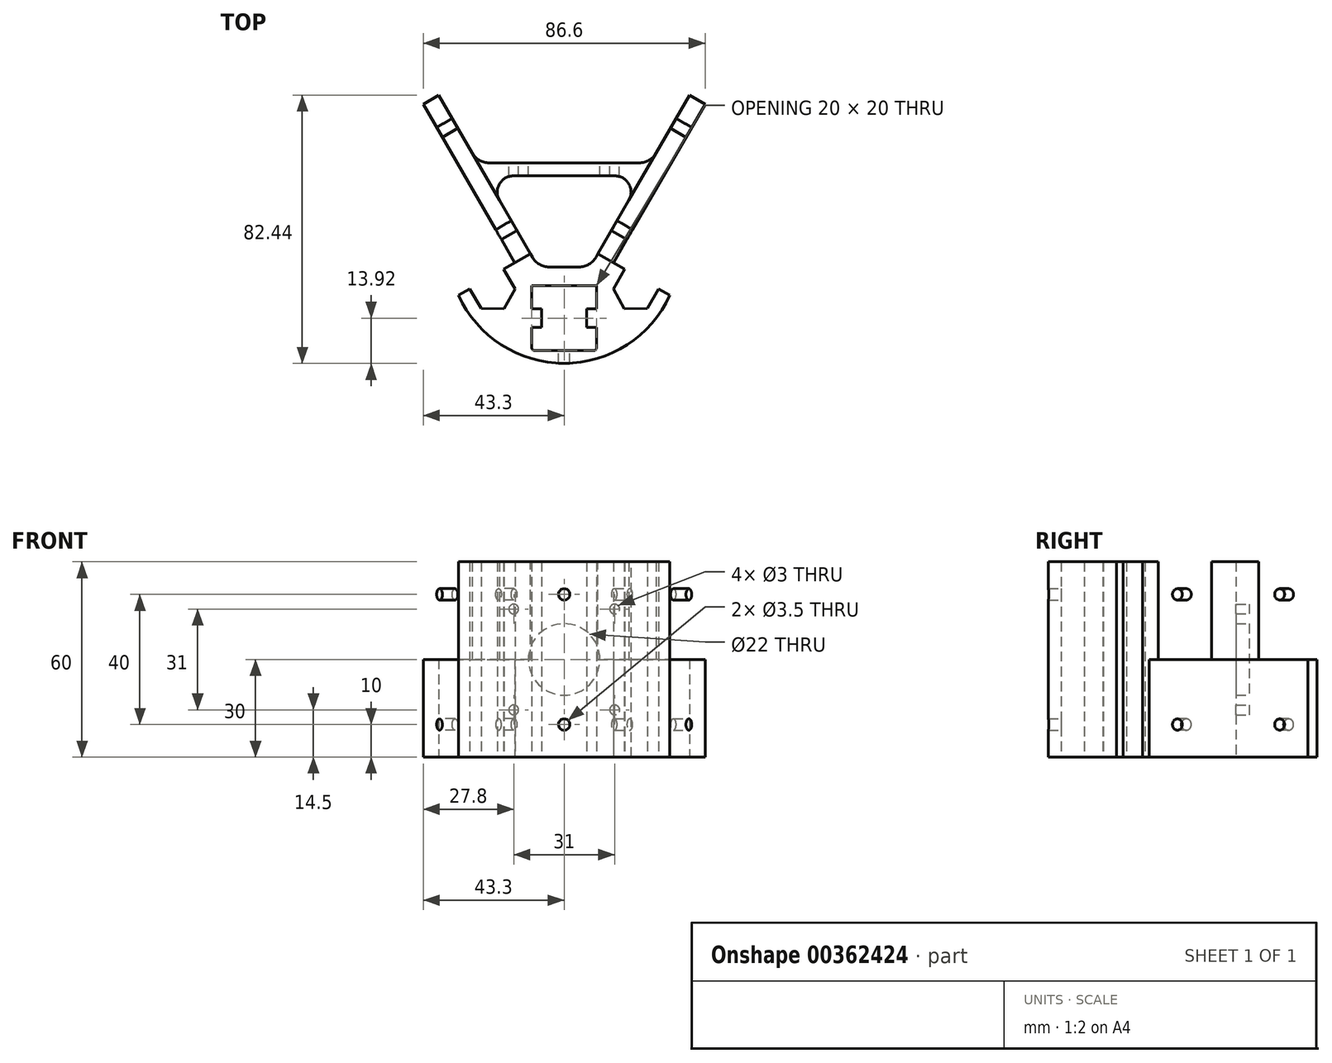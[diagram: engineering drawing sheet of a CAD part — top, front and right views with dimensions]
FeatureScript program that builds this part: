
annotation { "Feature Type Name" : "Feature", "Feature Type Description" : "" }
export const myFeature = defineFeature(function(context is Context, id is Id, definition is map)
    precondition{}
    {
        {
            var Q0;
            Q0=qCreatedBy(makeId("Top.planeOp"),FACE);
            var sketch = newSketch(context, id + "F0", { "sketchPlane" : qUnion([Q0])});
            skLineSegment(sketch, "E0", {"start": v(0, 0) * mm, "end": v(32.48, 0) * mm});
            skLineSegment(sketch, "E1", {"start": v(0, 0) * mm, "end": v(-32.48, 0) * mm});
            skArc(sketch, "E2", {"start": v(-32.48, 0) * mm, "mid": v(0, -20.94) * mm, "end": v(32.48, 0) * mm});
            skLineSegment(sketch, "E3", {"start": v(-32.48, 0) * mm, "end": v(-15.15, 10) * mm});
            skLineSegment(sketch, "E4", {"start": v(32.48, 0) * mm, "end": v(15.15, 10) * mm});
            skLineSegment(sketch, "E5", {"start": v(15.15, 10) * mm, "end": v(43.3, 58.75) * mm});
            skLineSegment(sketch, "E6", {"start": v(-15.15, 10) * mm, "end": v(-43.3, 58.75) * mm});
            skLineSegment(sketch, "E7", {"start": v(38.54, 61.5) * mm, "end": v(43.3, 58.75) * mm});
            skLineSegment(sketch, "E8.bottom", {"start": v(10, -17.02) * mm, "end": v(-10, -17.02) * mm});
            skLineSegment(sketch, "E8.top", {"start": v(10, 2.98) * mm, "end": v(-10, 2.98) * mm});
            skLineSegment(sketch, "E8.left", {"start": v(10, -17.02) * mm, "end": v(10, 2.98) * mm});
            skLineSegment(sketch, "E8.right", {"start": v(-10, -17.02) * mm, "end": v(-10, 2.98) * mm});
            skPoint(sketch, "E8.middle", {"position": v(0, -7.02) * mm});
            skLineSegment(sketch, "E9", {"start": v(-64.62, 8.7) * mm, "end": v(74.38, 8.7) * mm});
            skLineSegment(sketch, "E10", {"start": v(-43.3, 58.75) * mm, "end": v(-38.54, 61.5) * mm});
            skLineSegment(sketch, "E11", {"start": v(-38.54, 61.5) * mm, "end": v(-8.06, 8.7) * mm});
            skLineSegment(sketch, "E12", {"start": v(38.54, 61.5) * mm, "end": v(8.06, 8.7) * mm});
            skLineSegment(sketch, "E13", {"start": v(-64.62, 36.7) * mm, "end": v(67.86, 36.7) * mm});
            skLineSegment(sketch, "E14", {"start": v(-64.87, 40.7) * mm, "end": v(70.08, 40.7) * mm});
            skLineSegment(sketch, "E15.bottom", {"start": v(-10, -7.02) * mm, "end": v(-6.9, -7.02) * mm});
            skLineSegment(sketch, "E15.top", {"start": v(-10, -4.12) * mm, "end": v(-6.9, -4.12) * mm});
            skLineSegment(sketch, "E15.left", {"start": v(-10, -7.02) * mm, "end": v(-10, -4.12) * mm});
            skLineSegment(sketch, "E15.right", {"start": v(-6.9, -7.02) * mm, "end": v(-6.9, -4.12) * mm});
            skLineSegment(sketch, "E16.top", {"start": v(-10, -9.92) * mm, "end": v(-6.9, -9.92) * mm});
            skLineSegment(sketch, "E16.left", {"start": v(-10, -7.02) * mm, "end": v(-10, -9.92) * mm});
            skLineSegment(sketch, "E16.right", {"start": v(-6.9, -7.02) * mm, "end": v(-6.9, -9.92) * mm});
            skLineSegment(sketch, "E17.1.0", {"start": v(10, 2.98) * mm, "end": v(10, -17.02) * mm});
            skLineSegment(sketch, "E17.1.1", {"start": v(2.9, -17.02) * mm, "end": v(2.9, -13.92) * mm});
            skLineSegment(sketch, "E17.1.2", {"start": v(0, -17.02) * mm, "end": v(0, -13.92) * mm});
            skLineSegment(sketch, "E17.1.3", {"start": v(-2.9, -17.02) * mm, "end": v(-2.9, -13.92) * mm});
            skLineSegment(sketch, "E17.1.4", {"start": v(0, -13.92) * mm, "end": v(-2.9, -13.92) * mm});
            skLineSegment(sketch, "E17.1.5", {"start": v(0, -13.92) * mm, "end": v(2.9, -13.92) * mm});
            skLineSegment(sketch, "E17.2.0", {"start": v(-10, 2.98) * mm, "end": v(10, 2.98) * mm});
            skLineSegment(sketch, "E17.2.1", {"start": v(10, -4.12) * mm, "end": v(6.9, -4.12) * mm});
            skLineSegment(sketch, "E17.2.2", {"start": v(10, -7.02) * mm, "end": v(6.9, -7.02) * mm});
            skLineSegment(sketch, "E17.2.3", {"start": v(10, -9.92) * mm, "end": v(6.9, -9.92) * mm});
            skLineSegment(sketch, "E17.2.4", {"start": v(6.9, -7.02) * mm, "end": v(6.9, -9.92) * mm});
            skLineSegment(sketch, "E17.2.5", {"start": v(6.9, -7.02) * mm, "end": v(6.9, -4.12) * mm});
            skLineSegment(sketch, "E17.3.1", {"start": v(-2.9, 2.98) * mm, "end": v(-2.9, -0.12) * mm});
            skLineSegment(sketch, "E17.3.2", {"start": v(0, 2.98) * mm, "end": v(0, -0.12) * mm});
            skLineSegment(sketch, "E17.3.3", {"start": v(2.9, 2.98) * mm, "end": v(2.9, -0.12) * mm});
            skLineSegment(sketch, "E17.3.4", {"start": v(0, -0.12) * mm, "end": v(2.9, -0.12) * mm});
            skLineSegment(sketch, "E17.3.5", {"start": v(0, -0.12) * mm, "end": v(-2.9, -0.12) * mm});
            skLineSegment(sketch, "E18", {"start": v(18.62, 8) * mm, "end": v(15.12, 1.94) * mm});
            skLineSegment(sketch, "E19", {"start": v(29.01, 2) * mm, "end": v(25.51, -4.06) * mm});
            skPoint(sketch, "E20", {"position": v(23.81, 5) * mm});
            skLineSegment(sketch, "E21", {"start": v(15.12, 1.94) * mm, "end": v(18.51, -4.18) * mm});
            skLineSegment(sketch, "E22", {"start": v(25.51, -4.06) * mm, "end": v(18.51, -4.18) * mm});
            skLineSegment(sketch, "E23.MirrorCS", {"start": v(-18.62, 8) * mm, "end": v(-15.12, 1.94) * mm});
            skLineSegment(sketch, "E24.MirrorCS", {"start": v(-15.12, 1.94) * mm, "end": v(-18.51, -4.18) * mm});
            skLineSegment(sketch, "E25.MirrorCS", {"start": v(-25.51, -4.06) * mm, "end": v(-18.51, -4.18) * mm});
            skLineSegment(sketch, "E26.MirrorCS", {"start": v(-29.01, 2) * mm, "end": v(-25.51, -4.06) * mm});
            skSolve(sketch);
        }
        {
            var Q0;
            {var subQ0=sQuery(id+"F0.wireOp",EDGE,"E2");Q0=makeQuery(id+"F0.imprint","IMPRINT",FACE,{"disambiguationData":[TD([[makeQuery(id+"F0.imprint","IMPRINT",EDGE,{"derivedFrom":subQ0}),1.0]])]});}
            var Q1;
            {var subQ16=sQuery(id+"F0.wireOp",EDGE,"E8.top");Q1=makeQuery(id+"F0.imprint","IMPRINT",FACE,{"disambiguationData":[TD([[makeQuery(id+"F0.imprint","IMPRINT",EDGE,{"derivedFrom":subQ16}),-1.0]])]});}
            var Q2;
            {var subQ5=sQuery(id+"F0.wireOp",EDGE,"E5");var subQ6=sQuery(id+"F0.wireOp",EDGE,"E4");var subQ7=makeQuery(id+"F0.imprint","INTERSECT",VERTEX,{"derivedFrom":[subQ6,subQ5]});Q2=makeQuery(id+"F0.imprint","IMPRINT",FACE,{"disambiguationData":[TD([[makeQuery(id+"F0.imprint","IMPRINT",EDGE,{"disambiguationData":[TD([[subQ7,1.0]])],"derivedFrom":subQ6}),1.0]])]});}
            var Q3;
            {var subQ5=sQuery(id+"F0.wireOp",EDGE,"E6");var subQ6=sQuery(id+"F0.wireOp",EDGE,"E3");var subQ7=makeQuery(id+"F0.imprint","INTERSECT",VERTEX,{"derivedFrom":[subQ6,subQ5]});Q3=makeQuery(id+"F0.imprint","IMPRINT",FACE,{"disambiguationData":[TD([[makeQuery(id+"F0.imprint","IMPRINT",EDGE,{"disambiguationData":[TD([[subQ7,1.0]])],"derivedFrom":subQ6}),-1.0]])]});}
            var Q4;
            {var subQ0=sQuery(id+"F0.wireOp",EDGE,"E10");Q4=makeQuery(id+"F0.imprint","IMPRINT",FACE,{"disambiguationData":[TD([[makeQuery(id+"F0.imprint","IMPRINT",EDGE,{"derivedFrom":subQ0}),-1.0]])]});}
            var Q5;
            {var subQ0=sQuery(id+"F0.wireOp",EDGE,"E7");Q5=makeQuery(id+"F0.imprint","IMPRINT",FACE,{"disambiguationData":[TD([[makeQuery(id+"F0.imprint","IMPRINT",EDGE,{"derivedFrom":subQ0}),-1.0]])]});}
            var Q6;
            {var subQ0=sQuery(id+"F0.wireOp",EDGE,"E13");var subQ1=sQuery(id+"F0.wireOp",EDGE,"E5");var subQ2=makeQuery(id+"F0.imprint","INTERSECT",VERTEX,{"derivedFrom":[subQ1,subQ0]});Q6=makeQuery(id+"F0.imprint","IMPRINT",FACE,{"disambiguationData":[TD([[makeQuery(id+"F0.imprint","IMPRINT",EDGE,{"disambiguationData":[TD([[subQ2,-1.0]])],"derivedFrom":subQ1}),1.0]])]});}
            var Q7;
            {var subQ0=sQuery(id+"F0.wireOp",EDGE,"E14");var subQ1=sQuery(id+"F0.wireOp",EDGE,"E11");var subQ2=makeQuery(id+"F0.imprint","INTERSECT",VERTEX,{"derivedFrom":[subQ1,subQ0]});Q7=makeQuery(id+"F0.imprint","IMPRINT",FACE,{"disambiguationData":[TD([[makeQuery(id+"F0.imprint","IMPRINT",EDGE,{"disambiguationData":[TD([[subQ2,-1.0]])],"derivedFrom":subQ1}),1.0]])]});}
            var Q8;
            {var subQ0=sQuery(id+"F0.wireOp",EDGE,"E13");var subQ1=sQuery(id+"F0.wireOp",EDGE,"E6");var subQ2=makeQuery(id+"F0.imprint","INTERSECT",VERTEX,{"derivedFrom":[subQ1,subQ0]});Q8=makeQuery(id+"F0.imprint","IMPRINT",FACE,{"disambiguationData":[TD([[makeQuery(id+"F0.imprint","IMPRINT",EDGE,{"disambiguationData":[TD([[subQ2,-1.0]])],"derivedFrom":subQ1}),-1.0]])]});}
            var Q9;
            {var subQ11=sQuery(id+"F0.wireOp",EDGE,"E9");var subQ12=makeQuery(id+"F0.imprint","INTERSECT",VERTEX,{"derivedFrom":[subQ11,sQuery(id+"F0.wireOp",EDGE,"E11")]});Q9=makeQuery(id+"F0.imprint","IMPRINT",FACE,{"disambiguationData":[TD([[makeQuery(id+"F0.imprint","IMPRINT",EDGE,{"disambiguationData":[TD([[subQ12,1.0]])],"derivedFrom":subQ11}),-1.0]])]});}
            var Q10;
            {var subQ0=sQuery(id+"F0.wireOp",EDGE,"E17.3.2");var subQ5=sQuery(id+"F0.wireOp",EDGE,"E17.2.0");var subQ6=makeQuery(id+"F0.imprint","INTERSECT",VERTEX,{"derivedFrom":[subQ5,subQ0]});Q10=makeQuery(id+"F0.imprint","IMPRINT",FACE,{"disambiguationData":[TD([[makeQuery(id+"F0.imprint","IMPRINT",EDGE,{"disambiguationData":[TD([[subQ6,-1.0]])],"derivedFrom":subQ5}),-1.0]])]});}
            var Q11;
            {var subQ3=sQuery(id+"F0.wireOp",EDGE,"E17.3.1");var subQ5=sQuery(id+"F0.wireOp",EDGE,"E17.2.0");var subQ6=makeQuery(id+"F0.imprint","INTERSECT",VERTEX,{"derivedFrom":[subQ5,subQ3]});Q11=makeQuery(id+"F0.imprint","IMPRINT",FACE,{"disambiguationData":[TD([[makeQuery(id+"F0.imprint","IMPRINT",EDGE,{"disambiguationData":[TD([[subQ6,-1.0]])],"derivedFrom":subQ5}),-1.0]])]});}
            var Q12;
            {var subQ0=sQuery(id+"F0.wireOp",EDGE,"E15.bottom");Q12=makeQuery(id+"F0.imprint","IMPRINT",FACE,{"disambiguationData":[TD([[makeQuery(id+"F0.imprint","IMPRINT",EDGE,{"derivedFrom":subQ0}),-1.0]])]});}
            var Q13;
            {var subQ0=sQuery(id+"F0.wireOp",EDGE,"E15.top");Q13=makeQuery(id+"F0.imprint","IMPRINT",FACE,{"disambiguationData":[TD([[makeQuery(id+"F0.imprint","IMPRINT",EDGE,{"derivedFrom":subQ0}),-1.0]])]});}
            var Q14;
            {var subQ0=sQuery(id+"F0.wireOp",EDGE,"E17.2.1");Q14=makeQuery(id+"F0.imprint","IMPRINT",FACE,{"disambiguationData":[TD([[makeQuery(id+"F0.imprint","IMPRINT",EDGE,{"derivedFrom":subQ0}),1.0]])]});}
            var Q15;
            {var subQ0=sQuery(id+"F0.wireOp",EDGE,"E17.2.2");Q15=makeQuery(id+"F0.imprint","IMPRINT",FACE,{"disambiguationData":[TD([[makeQuery(id+"F0.imprint","IMPRINT",EDGE,{"derivedFrom":subQ0}),1.0]])]});}
            var Q16;
            {var subQ0=sQuery(id+"F0.wireOp",EDGE,"E3");var subQ3=sQuery(id+"F0.wireOp",EDGE,"E26.MirrorCS");var subQ5=makeQuery(id+"F0.imprint","INTERSECT",VERTEX,{"derivedFrom":[subQ0,subQ3]});Q16=makeQuery(id+"F0.imprint","IMPRINT",FACE,{"disambiguationData":[TD([[makeQuery(id+"F0.imprint","IMPRINT",EDGE,{"disambiguationData":[TD([[subQ5,-1.0]])],"derivedFrom":subQ3}),-1.0]])]});}
            var Q17;
            {var subQ0=sQuery(id+"F0.wireOp",EDGE,"E4");var subQ3=sQuery(id+"F0.wireOp",EDGE,"E19");var subQ5=makeQuery(id+"F0.imprint","INTERSECT",VERTEX,{"derivedFrom":[subQ0,subQ3]});Q17=makeQuery(id+"F0.imprint","IMPRINT",FACE,{"disambiguationData":[TD([[makeQuery(id+"F0.imprint","IMPRINT",EDGE,{"disambiguationData":[TD([[subQ5,-1.0]])],"derivedFrom":subQ3}),1.0]])]});}
            extrude(context, id + "F1", {"entities" : qUnion([Q0, Q1, Q2, Q3, Q4, Q5, Q6, Q7, Q8, Q9, Q10, Q11, Q12, Q13, Q14, Q15, Q16, Q17]), "depth" : 60 * mm});
        }
        {
            var Q0;
            Q0=makeQuery(id+"F1.opExtrude","SWEPT_EDGE",EDGE,{"disambiguationData":[OSD([sQuery(id+"F0.wireOp",EDGE,"E9"),sQuery(id+"F0.wireOp",EDGE,"E11")])]});
            var Q1;
            Q1=makeQuery(id+"F1.opExtrude","SWEPT_EDGE",EDGE,{"disambiguationData":[OSD([sQuery(id+"F0.wireOp",EDGE,"E9"),sQuery(id+"F0.wireOp",EDGE,"E12")])]});
            var Q2;
            Q2=makeQuery(id+"F1.opExtrude","SWEPT_EDGE",EDGE,{"disambiguationData":[OSD([sQuery(id+"F0.wireOp",EDGE,"E12"),sQuery(id+"F0.wireOp",EDGE,"E14")])]});
            var Q3;
            Q3=makeQuery(id+"F1.opExtrude","SWEPT_EDGE",EDGE,{"disambiguationData":[OSD([sQuery(id+"F0.wireOp",EDGE,"E11"),sQuery(id+"F0.wireOp",EDGE,"E14")])]});
            fillet(context, id + "F2", {"entities" : qUnion([Q0, Q1, Q2, Q3]), "radius" : 6 * mm, "tangentPropagation" : true, "allowEdgeOverflow" : false});
        }
        {
            var Q0;
            Q0=makeQuery(id+"F1.opExtrude","SWEPT_EDGE",EDGE,{"disambiguationData":[OSD([sQuery(id+"F0.wireOp",EDGE,"E8.bottom"),sQuery(id+"F0.wireOp",EDGE,"E8.right")])]});
            var Q1;
            Q1=makeQuery(id+"F1.opExtrude","SWEPT_EDGE",EDGE,{"disambiguationData":[OSD([sQuery(id+"F0.wireOp",EDGE,"E8.bottom"),sQuery(id+"F0.wireOp",EDGE,"E17.1.0")])]});
            var Q2;
            Q2=makeQuery(id+"F1.opExtrude","SWEPT_EDGE",EDGE,{"disambiguationData":[OSD([sQuery(id+"F0.wireOp",EDGE,"E17.1.0"),sQuery(id+"F0.wireOp",EDGE,"E17.2.0")])]});
            var Q3;
            Q3=makeQuery(id+"F1.opExtrude","SWEPT_EDGE",EDGE,{"disambiguationData":[OSD([sQuery(id+"F0.wireOp",EDGE,"E17.2.0"),sQuery(id+"F0.wireOp",EDGE,"E8.right")])]});
            fillet(context, id + "F3", {"entities" : qUnion([Q0, Q1, Q2, Q3]), "radius" : 1 * mm, "tangentPropagation" : true, "allowEdgeOverflow" : false});
        }
        {
            var Q0;
            Q0=makeQuery(id+"F1.opExtrude","SWEPT_EDGE",EDGE,{"disambiguationData":[OSD([sQuery(id+"F0.wireOp",EDGE,"E11"),sQuery(id+"F0.wireOp",EDGE,"E13")])]});
            var Q1;
            Q1=makeQuery(id+"F1.opExtrude","SWEPT_EDGE",EDGE,{"disambiguationData":[OSD([sQuery(id+"F0.wireOp",EDGE,"E12"),sQuery(id+"F0.wireOp",EDGE,"E13")])]});
            fillet(context, id + "F4", {"entities" : qUnion([Q0, Q1]), "radius" : 5 * mm, "tangentPropagation" : true, "allowEdgeOverflow" : false});
        }
        {
            var Q0;
            Q0=makeQuery(id+"F1.opExtrude","SWEPT_FACE",FACE,{"disambiguationData":[OSD([sQuery(id+"F0.wireOp",EDGE,"E5")])]});
            var sketch = newSketch(context, id + "F5", { "sketchPlane" : qUnion([Q0])});
            skCircle(sketch, "E27", {"center": v(26.24, 10) * mm, "radius": 1.75 * mm});
            skCircle(sketch, "E28", {"center": v(62.53, 10) * mm, "radius": 1.75 * mm});
            skLineSegment(sketch, "E29", {"start": v(16.24, 30) * mm, "end": v(72.53, 30) * mm});
            skCircle(sketch, "E30.MirrorC", {"center": v(26.24, 50) * mm, "radius": 1.75 * mm});
            skCircle(sketch, "E31.MirrorC", {"center": v(62.53, 50) * mm, "radius": 1.75 * mm});
            skSolve(sketch);
        }
        {
            var Q0;
            Q0=makeQuery(id+"F5.imprint","IMPRINT",FACE,{"disambiguationData":[TD([[makeQuery(id+"F5.imprint","IMPRINT",EDGE,{"derivedFrom":sQuery(id+"F5.wireOp",EDGE,"E30.MirrorC")}),-1.0]])]});
            var Q1;
            Q1=makeQuery(id+"F5.imprint","IMPRINT",FACE,{"disambiguationData":[TD([[makeQuery(id+"F5.imprint","IMPRINT",EDGE,{"derivedFrom":sQuery(id+"F5.wireOp",EDGE,"E31.MirrorC")}),-1.0]])]});
            var Q2;
            Q2=makeQuery(id+"F5.imprint","IMPRINT",FACE,{"disambiguationData":[TD([[makeQuery(id+"F5.imprint","IMPRINT",EDGE,{"derivedFrom":sQuery(id+"F5.wireOp",EDGE,"E27")}),1.0]])]});
            var Q3;
            Q3=makeQuery(id+"F5.imprint","IMPRINT",FACE,{"disambiguationData":[TD([[makeQuery(id+"F5.imprint","IMPRINT",EDGE,{"derivedFrom":sQuery(id+"F5.wireOp",EDGE,"E28")}),1.0]])]});
            var Q4;
            {var subQ0=sQuery(id+"F0.wireOp",EDGE,"E12");Q4=makeQuery(id+"F1.opExtrude","SWEPT_FACE",FACE,{"disambiguationData":[OSD([subQ0]),TDD([makeQuery(id+"F0.imprint","IMPRINT",EDGE,{"disambiguationData":[TD([[makeQuery(id+"F0.imprint","INTERSECT",VERTEX,{"derivedFrom":[sQuery(id+"F0.wireOp",EDGE,"E9"),subQ0]}),1.0]])],"derivedFrom":subQ0})])]});}
            extrude(context, id + "F6", {"entities" : qUnion([Q0, Q1, Q2, Q3]), "operationType" : NewBodyOperationType.REMOVE, "endBound" : BoundingType.UP_TO_SURFACE, "oppositeDirection" : true, "endBoundEntityFace" : qUnion([Q4]), "depth" : 25 * mm});
        }
        {
            var Q0;
            Q0=makeQuery(id+"F1.opExtrude","SWEPT_FACE",FACE,{"disambiguationData":[OSD([sQuery(id+"F0.wireOp",EDGE,"E8.bottom")])]});
            var sketch = newSketch(context, id + "F7", { "sketchPlane" : qUnion([Q0])});
            skCircle(sketch, "E32", {"center": v(0, 50) * mm, "radius": 1.75 * mm});
            skPoint(sketch, "E32.centerSnap0", {"position": v(0, 60) * mm});
            skCircle(sketch, "E33", {"center": v(0, 10) * mm, "radius": 1.75 * mm});
            skSolve(sketch);
        }
        {
            var Q0;
            Q0 = qSketchRegion(id + "F7", true);
            var Q1;
            Q1=makeQuery(id+"F1.opExtrude","SWEPT_FACE",FACE,{"disambiguationData":[OSD([sQuery(id+"F0.wireOp",EDGE,"E2")])]});
            extrude(context, id + "F8", {"entities" : qUnion([Q0]), "operationType" : NewBodyOperationType.REMOVE, "endBound" : BoundingType.UP_TO_SURFACE, "oppositeDirection" : true, "endBoundEntityFace" : qUnion([Q1]), "depth" : 25 * mm});
        }
        {
            var Q0;
            Q0=makeQuery(id+"F1.opExtrude","SWEPT_BODY",BODY,{"disambiguationData":[OSD([sQuery(id+"F0.wireOp",EDGE,"E0"),sQuery(id+"F0.wireOp",EDGE,"E1"),sQuery(id+"F0.wireOp",EDGE,"E2"),sQuery(id+"F0.wireOp",EDGE,"E3"),sQuery(id+"F0.wireOp",EDGE,"E4"),sQuery(id+"F0.wireOp",EDGE,"E5"),sQuery(id+"F0.wireOp",EDGE,"E6"),sQuery(id+"F0.wireOp",EDGE,"E7"),sQuery(id+"F0.wireOp",EDGE,"E8.bottom"),sQuery(id+"F0.wireOp",EDGE,"E9"),sQuery(id+"F0.wireOp",EDGE,"E10"),sQuery(id+"F0.wireOp",EDGE,"E11"),sQuery(id+"F0.wireOp",EDGE,"E12"),sQuery(id+"F0.wireOp",EDGE,"E13"),sQuery(id+"F0.wireOp",EDGE,"E14"),sQuery(id+"F0.wireOp",EDGE,"E15.top"),sQuery(id+"F0.wireOp",EDGE,"E15.right"),sQuery(id+"F0.wireOp",EDGE,"E16.top"),sQuery(id+"F0.wireOp",EDGE,"E16.right"),sQuery(id+"F0.wireOp",EDGE,"E17.1.0"),sQuery(id+"F0.wireOp",EDGE,"E17.2.0"),sQuery(id+"F0.wireOp",EDGE,"E17.2.1"),sQuery(id+"F0.wireOp",EDGE,"E17.2.3"),sQuery(id+"F0.wireOp",EDGE,"E17.2.4"),sQuery(id+"F0.wireOp",EDGE,"E17.2.5"),sQuery(id+"F0.wireOp",EDGE,"E8.right"),sQuery(id+"F0.wireOp",EDGE,"E17.3.1"),sQuery(id+"F0.wireOp",EDGE,"E17.3.3"),sQuery(id+"F0.wireOp",EDGE,"E18"),sQuery(id+"F0.wireOp",EDGE,"E19"),sQuery(id+"F0.wireOp",EDGE,"E21"),sQuery(id+"F0.wireOp",EDGE,"E22"),sQuery(id+"F0.wireOp",EDGE,"E23.MirrorCS"),sQuery(id+"F0.wireOp",EDGE,"E24.MirrorCS"),sQuery(id+"F0.wireOp",EDGE,"E25.MirrorCS"),sQuery(id+"F0.wireOp",EDGE,"E26.MirrorCS")])]});
            transform(context, id + "F9", {"entities" : qUnion([Q0]), "transformType" : TransformType.TRANSLATION_3D, "dx" : 0 * mm, "dy" : 7.02 * mm, "dz" : 0 * mm, "makeCopy" : false});
        }
        {
            var Q0;
            Q0=makeQuery(id+"F1.opExtrude","SWEPT_FACE",FACE,{"disambiguationData":[OSD([sQuery(id+"F0.wireOp",EDGE,"E14")])]});
            var sketch = newSketch(context, id + "F10", { "sketchPlane" : qUnion([Q0])});
            skCircle(sketch, "E34", {"center": v(0, 30) * mm, "radius": 11 * mm});
            skCircle(sketch, "E35", {"center": v(-15.5, 45.5) * mm, "radius": 1.5 * mm});
            skCircle(sketch, "E36", {"center": v(-15.5, 14.5) * mm, "radius": 1.5 * mm});
            skSolve(sketch);
        }
        {
            var Q0;
            Q0=makeQuery(id+"F10.imprint","IMPRINT",FACE,{"disambiguationData":[TD([[makeQuery(id+"F10.imprint","IMPRINT",EDGE,{"derivedFrom":sQuery(id+"F10.wireOp",EDGE,"E34")}),1.0]])]});
            var Q1;
            Q1=makeQuery(id+"F10.imprint","IMPRINT",FACE,{"disambiguationData":[TD([[makeQuery(id+"F10.imprint","IMPRINT",EDGE,{"derivedFrom":sQuery(id+"F10.wireOp",EDGE,"E35")}),1.0]])]});
            var Q2;
            Q2=makeQuery(id+"F10.imprint","IMPRINT",FACE,{"disambiguationData":[TD([[makeQuery(id+"F10.imprint","IMPRINT",EDGE,{"derivedFrom":sQuery(id+"F10.wireOp",EDGE,"E36")}),1.0]])]});
            var Q3;
            Q3=makeQuery(id+"F1.opExtrude","SWEPT_FACE",FACE,{"disambiguationData":[OSD([sQuery(id+"F0.wireOp",EDGE,"E13")])]});
            extrude(context, id + "F11", {"entities" : qUnion([Q0, Q1, Q2]), "operationType" : NewBodyOperationType.REMOVE, "oppositeDirection" : true, "endBoundEntityFace" : qUnion([Q3]), "depth" : 10 * mm});
        }
        {
            var Q0;
            Q0=makeQuery(id+"F1.opExtrude","SWEPT_BODY",BODY,{"disambiguationData":[OSD([sQuery(id+"F0.wireOp",EDGE,"E0"),sQuery(id+"F0.wireOp",EDGE,"E1"),sQuery(id+"F0.wireOp",EDGE,"E2"),sQuery(id+"F0.wireOp",EDGE,"E3"),sQuery(id+"F0.wireOp",EDGE,"E4"),sQuery(id+"F0.wireOp",EDGE,"E5"),sQuery(id+"F0.wireOp",EDGE,"E6"),sQuery(id+"F0.wireOp",EDGE,"E7"),sQuery(id+"F0.wireOp",EDGE,"E8.bottom"),sQuery(id+"F0.wireOp",EDGE,"E9"),sQuery(id+"F0.wireOp",EDGE,"E10"),sQuery(id+"F0.wireOp",EDGE,"E11"),sQuery(id+"F0.wireOp",EDGE,"E12"),sQuery(id+"F0.wireOp",EDGE,"E13"),sQuery(id+"F0.wireOp",EDGE,"E14"),sQuery(id+"F0.wireOp",EDGE,"E15.top"),sQuery(id+"F0.wireOp",EDGE,"E15.right"),sQuery(id+"F0.wireOp",EDGE,"E16.top"),sQuery(id+"F0.wireOp",EDGE,"E16.right"),sQuery(id+"F0.wireOp",EDGE,"E17.1.0"),sQuery(id+"F0.wireOp",EDGE,"E17.2.0"),sQuery(id+"F0.wireOp",EDGE,"E17.2.1"),sQuery(id+"F0.wireOp",EDGE,"E17.2.3"),sQuery(id+"F0.wireOp",EDGE,"E17.2.4"),sQuery(id+"F0.wireOp",EDGE,"E17.2.5"),sQuery(id+"F0.wireOp",EDGE,"E8.right"),sQuery(id+"F0.wireOp",EDGE,"E17.3.1"),sQuery(id+"F0.wireOp",EDGE,"E17.3.3"),sQuery(id+"F0.wireOp",EDGE,"E18"),sQuery(id+"F0.wireOp",EDGE,"E19"),sQuery(id+"F0.wireOp",EDGE,"E21"),sQuery(id+"F0.wireOp",EDGE,"E22"),sQuery(id+"F0.wireOp",EDGE,"E23.MirrorCS"),sQuery(id+"F0.wireOp",EDGE,"E24.MirrorCS"),sQuery(id+"F0.wireOp",EDGE,"E25.MirrorCS"),sQuery(id+"F0.wireOp",EDGE,"E26.MirrorCS")])]});
            var Q1;
            Q1=qCreatedBy(makeId("Right.planeOp"),FACE);
            mirror(context, id + "F12", {"operationType" : NewBodyOperationType.INTERSECT, "entities" : qUnion([Q0]), "mirrorPlane" : qUnion([Q1])});
        }
    });
